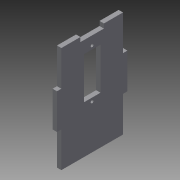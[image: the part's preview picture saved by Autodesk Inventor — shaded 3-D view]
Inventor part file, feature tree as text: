
AUTODESK INVENTOR PART (.ipt)
format: ipt  version: 2013 (Build 170138000, 138)  size: 120,832 bytes
history: native  units: in
note: dims shown in document units (in); Inventor stores cm internally (conversion verified against a paired STEP export)
features: extrude x4, sketch x4
ambient origin geometry x8: Origin, YZ Plane, XZ Plane, XY Plane, X Axis, Y Axis, Z Axis, Center Point
bodies: Solid1 (feature_tree)
feature tree (8):
  extrude  "Extrusion1"  Depth=1.75in
  extrude  "Extrusion2"  TaperAngle=0.0deg  [1 undecoded]
  extrude  "Extrusion3"  Depth=0.125in
  extrude  "Extrusion4"  TaperAngle=0.0deg  [1 undecoded]
  sketch  "Sketch1"  dims[d0=3.0in d1=1.75in]
  sketch  "Sketch2"  dims[d2=0.125in d3=0.0in]
  sketch  "Sketch3"  dims[d4=0.6667in d5=0.125in]
  sketch  "Sketch4"  dims[d6=0.125in d7=0.0in d8=0.5417in d9=0.125in d10=1.0in d11=1.0in d12=0.125in d13=1.0in d14=0.125in d15=0.0in d16=0.4724in d17=1.1811in d19=0.7638in d20=0.4724in d21=0.083in d22=0.2362in d23=0.0984in d24=0.083in d25=0.2362in d26=0.0984in d27=0.125in d28=0.0in]
note: 2 required parameter values undecoded (feature->parameter linkage not recoverable at this tier; creation-order binding heuristic only, values carry confidence <= 0.55)
